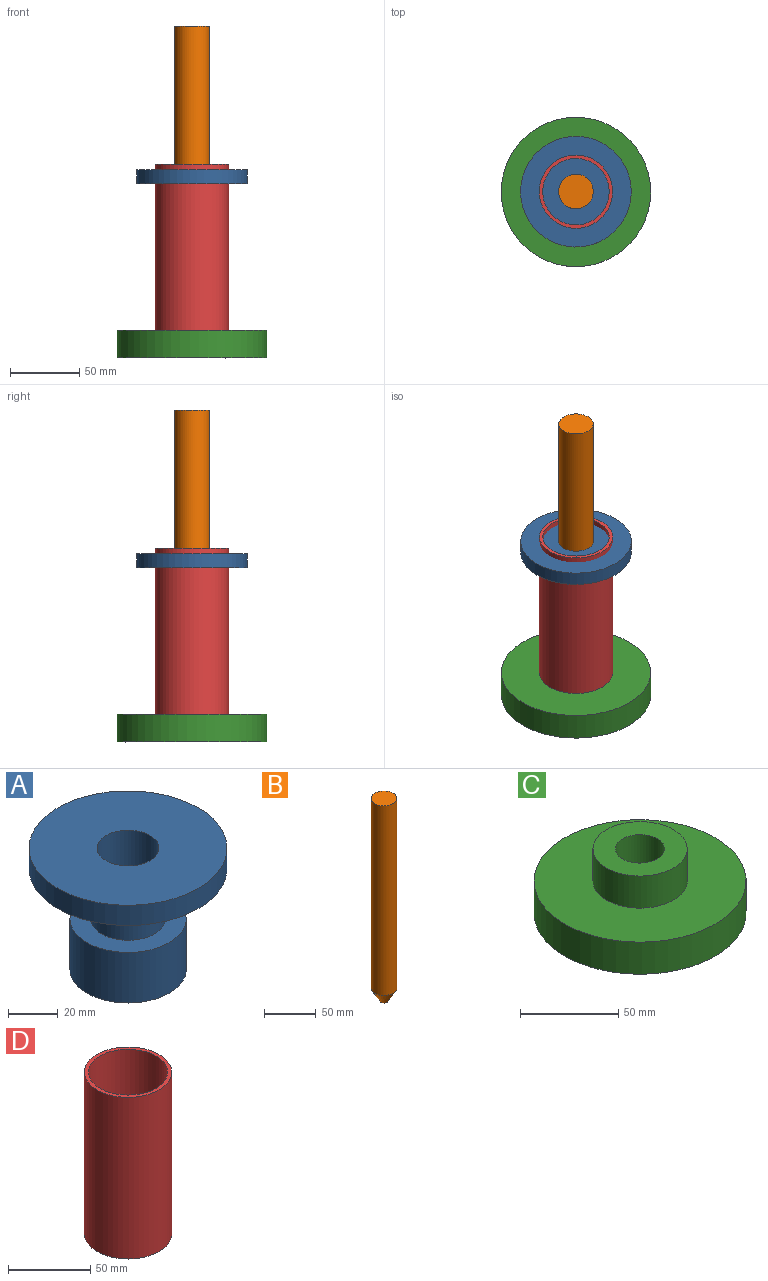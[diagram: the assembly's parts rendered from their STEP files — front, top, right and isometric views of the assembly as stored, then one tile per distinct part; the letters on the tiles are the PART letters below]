
ASSEMBLY  parts=4 mates=3
PART A: 8 faces, bbox 80x80x60 mm
  f0: cylinder r=40mm len=80mm, axis (0,0,1), area 2513.3mm2, adj f1,f6
  f1: plane 80x80mm, normal (0,0,-1), area 4319.7mm2, adj f0,f2
  f2: cylinder r=15mm len=30mm, axis (0,0,1), area 2356.2mm2, adj f1,f3
  f3: plane 47x47mm, normal (0,0,1), area 1028.1mm2, adj f2,f4
  f4: cylinder r=23.5mm len=47mm, axis (0,0,1), area 3691.4mm2, adj f3,f5
  f5: plane 47x47mm, normal (0,0,-1), area 1244.1mm2, adj f4,f7
  f6: plane 80x80mm, normal (0,0,1), area 4535.7mm2, adj f0,f7
  f7: cylinder r=12.5mm len=60mm, axis (0,0,-1), area 4712.4mm2, adj f5,f6
PART B: 4 faces, bbox 25x25x240 mm
  f0: plane 7.68x7.68mm, normal (0,0,-1), area 46.3mm2, adj f3
  f1: plane 25x25mm, normal (0,0,1), area 490.9mm2, adj f2
  f2: cylinder r=12.5mm len=225mm, axis (0,0,1), area 17671.5mm2, adj f1,f3
  f3: cone r=3.84mm half-angle=30deg, axis (0,0,1), area 889.1mm2, adj f0,f2
PART C: 6 faces, bbox 108x108x40 mm
  f0: plane 108x108mm, normal (0,0,-1), area 8670mm2, adj f4,f5
  f1: plane 48x48mm, normal (0,0,1), area 1318.7mm2, adj f2,f5
  f2: cylinder r=24mm len=48mm, axis (0,0,1), area 3015.9mm2, adj f1,f3
  f3: plane 108x108mm, normal (0,0,1), area 7351.3mm2, adj f2,f4
  f4: cylinder r=54mm len=108mm, axis (0,0,1), area 6785.8mm2, adj f0,f3
  f5: cylinder r=12.5mm len=40mm, axis (0,0,-1), area 3141.6mm2, adj f0,f1
PART D: 4 faces, bbox 53x53x120 mm
  f0: cylinder r=24mm len=120mm, axis (0,0,-1), area 18095.6mm2, adj f2,f3
  f1: cylinder r=26.5mm len=120mm, axis (0,0,-1), area 19980.5mm2, adj f2,f3
  f2: plane 53x53mm, normal (0,0,1), area 396.6mm2, adj f0,f1
  f3: plane 53x53mm, normal (0,0,-1), area 396.6mm2, adj f0,f1
PLACE A rot(axis=(-0.81,0.43,-0.4),0deg) t=(-49.41,37.35,48.88)mm
PLACE B rot(axis=(-0.81,0.43,-0.4),0deg) t=(-49.41,37.35,-12.26)mm
PLACE C rot(axis=(-0.81,0.43,-0.4),0deg) t=(-49.41,37.35,-27.26)mm
PLACE D rot(axis=(-0.81,0.43,-0.4),0deg) t=(-49.41,37.35,-7.26)mm
MATE fastened B.f2 <-> C.f2  axis (0,0,-1) through (-49.41,37.35,-27.26)mm
MATE fastened D.f0 <-> C.f2  axis (0,0,-1) through (-49.41,37.35,-7.26)mm
MATE slider A.f0 <-> D.f1  axis (0,0,1) through (-49.41,37.35,98.88)mm
